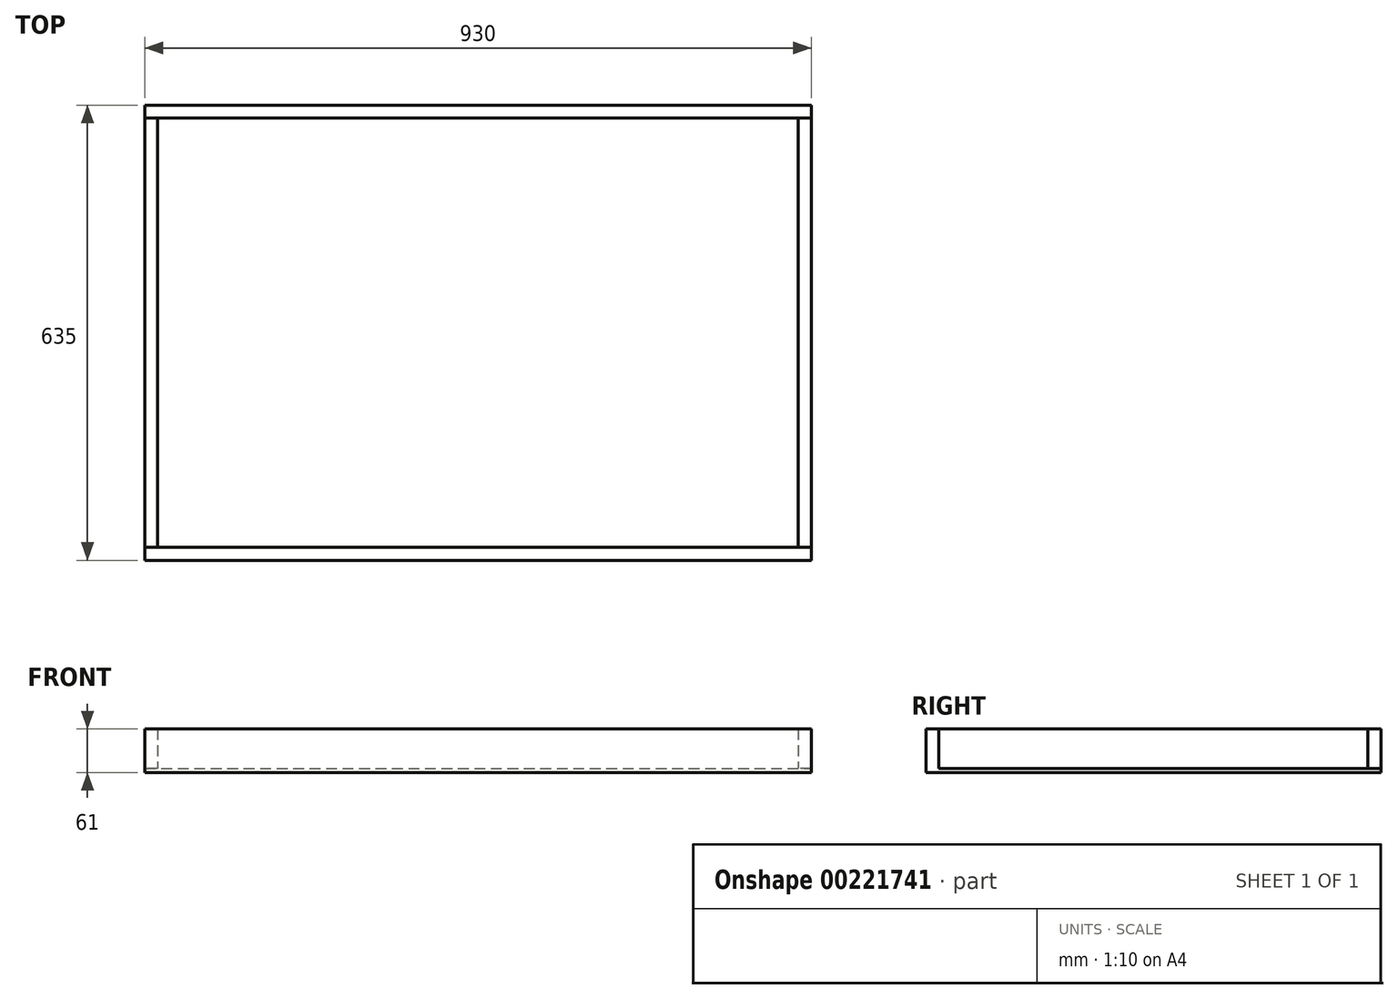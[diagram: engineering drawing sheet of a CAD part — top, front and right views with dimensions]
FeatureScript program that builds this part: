
annotation { "Feature Type Name" : "Feature", "Feature Type Description" : "" }
export const myFeature = defineFeature(function(context is Context, id is Id, definition is map)
    precondition{}
    {
        {
            var Q0;
            Q0=qCreatedBy(makeId("Top.planeOp"),FACE);
            var sketch = newSketch(context, id + "F0", { "sketchPlane" : qUnion([Q0])});
            skLineSegment(sketch, "E0.bottom", {"start": v(465, 317.5) * mm, "end": v(-465, 317.5) * mm});
            skLineSegment(sketch, "E0.top", {"start": v(465, -317.5) * mm, "end": v(-465, -317.5) * mm});
            skLineSegment(sketch, "E0.left", {"start": v(465, 317.5) * mm, "end": v(465, -317.5) * mm});
            skLineSegment(sketch, "E0.right", {"start": v(-465, 317.5) * mm, "end": v(-465, -317.5) * mm});
            skPoint(sketch, "E0.middle", {"position": v(0, 0) * mm});
            skSolve(sketch);
        }
        {
            var Q0;
            Q0 = qSketchRegion(id + "F0", true);
            extrude(context, id + "F1", {"entities" : qUnion([Q0]), "depth" : 6 * mm});
        }
        {
            var Q0;
            Q0=makeQuery(id+"F1.opExtrude","SWEPT_FACE",FACE,{"disambiguationData":[OSD([sQuery(id+"F0.wireOp",EDGE,"E0.left")])]});
            var sketch = newSketch(context, id + "F2", { "sketchPlane" : qUnion([Q0])});
            skLineSegment(sketch, "E1.bottom", {"start": v(-317.5, 6) * mm, "end": v(-299.5, 6) * mm});
            skLineSegment(sketch, "E1.top", {"start": v(-317.5, 61) * mm, "end": v(-299.5, 61) * mm});
            skLineSegment(sketch, "E1.left", {"start": v(-317.5, 6) * mm, "end": v(-317.5, 61) * mm});
            skLineSegment(sketch, "E1.right", {"start": v(-299.5, 6) * mm, "end": v(-299.5, 61) * mm});
            skSolve(sketch);
        }
        {
            var Q0;
            Q0 = qSketchRegion(id + "F2", true);
            extrude(context, id + "F3", {"entities" : qUnion([Q0]), "operationType" : NewBodyOperationType.ADD, "oppositeDirection" : true, "depth" : 930 * mm});
        }
        {
            var Q0;
            Q0=makeQuery(id+"F3.boolean.opBoolean","MERGE",FACE,{"derivedFrom":[makeQuery(id+"F1.opExtrude","SWEPT_FACE",FACE,{"disambiguationData":[OSD([sQuery(id+"F0.wireOp",EDGE,"E0.left")])]}),makeQuery(id+"F3.opExtrude","CAP_FACE",FACE,{"disambiguationData":[OSD([sQuery(id+"F2.wireOp",EDGE,"E1.bottom"),sQuery(id+"F2.wireOp",EDGE,"E1.top"),sQuery(id+"F2.wireOp",EDGE,"E1.left"),sQuery(id+"F2.wireOp",EDGE,"E1.right")])],"isStart":true})]});
            var sketch = newSketch(context, id + "F4", { "sketchPlane" : qUnion([Q0])});
            skLineSegment(sketch, "E2.bottom", {"start": v(317.5, 6) * mm, "end": v(299.5, 6) * mm});
            skLineSegment(sketch, "E2.top", {"start": v(317.5, 61) * mm, "end": v(299.5, 61) * mm});
            skLineSegment(sketch, "E2.left", {"start": v(317.5, 6) * mm, "end": v(317.5, 61) * mm});
            skLineSegment(sketch, "E2.right", {"start": v(299.5, 6) * mm, "end": v(299.5, 61) * mm});
            skSolve(sketch);
        }
        {
            var Q0;
            Q0 = qSketchRegion(id + "F4", true);
            extrude(context, id + "F5", {"entities" : qUnion([Q0]), "oppositeDirection" : true, "depth" : 930 * mm});
        }
        {
            var Q0;
            Q0=makeQuery(id+"F5.opExtrude","SWEPT_FACE",FACE,{"disambiguationData":[OSD([sQuery(id+"F4.wireOp",EDGE,"E2.right")])]});
            var sketch = newSketch(context, id + "F6", { "sketchPlane" : qUnion([Q0])});
            skLineSegment(sketch, "E3.0", {"start": v(465, 6) * mm, "end": v(465, 61) * mm});
            skLineSegment(sketch, "E4.0", {"start": v(-465, 61) * mm, "end": v(465, 61) * mm});
            skLineSegment(sketch, "E5.0", {"start": v(-465, 6) * mm, "end": v(465, 6) * mm});
            skLineSegment(sketch, "E6", {"start": v(447, 6) * mm, "end": v(447, 61) * mm});
            skSolve(sketch);
        }
        {
            var Q0;
            Q0 = qSketchRegion(id + "F6", true);
            var Q1;
            Q1=makeQuery(id+"F3.opExtrude","SWEPT_FACE",FACE,{"disambiguationData":[OSD([sQuery(id+"F2.wireOp",EDGE,"E1.right")])]});
            extrude(context, id + "F7", {"entities" : qUnion([Q0]), "endBound" : BoundingType.UP_TO_SURFACE, "endBoundEntityFace" : qUnion([Q1]), "depth" : 25 * mm});
        }
        {
            var Q0;
            Q0=makeQuery(id+"F5.opExtrude","SWEPT_FACE",FACE,{"disambiguationData":[OSD([sQuery(id+"F4.wireOp",EDGE,"E2.right")])]});
            var sketch = newSketch(context, id + "F8", { "sketchPlane" : qUnion([Q0])});
            skLineSegment(sketch, "E7.0", {"start": v(-465, 6) * mm, "end": v(465, 6) * mm});
            skLineSegment(sketch, "E8.0", {"start": v(-465, 6) * mm, "end": v(-465, 61) * mm});
            skLineSegment(sketch, "E9.0", {"start": v(-465, 61) * mm, "end": v(465, 61) * mm});
            skLineSegment(sketch, "E10", {"start": v(-447, 6) * mm, "end": v(-447, 61) * mm});
            skSolve(sketch);
        }
        {
            var Q0;
            Q0 = qSketchRegion(id + "F8", true);
            var Q1;
            Q1=makeQuery(id+"F3.opExtrude","SWEPT_FACE",FACE,{"disambiguationData":[OSD([sQuery(id+"F2.wireOp",EDGE,"E1.right")])]});
            extrude(context, id + "F9", {"entities" : qUnion([Q0]), "endBound" : BoundingType.UP_TO_SURFACE, "endBoundEntityFace" : qUnion([Q1]), "depth" : 25 * mm});
        }
    });
